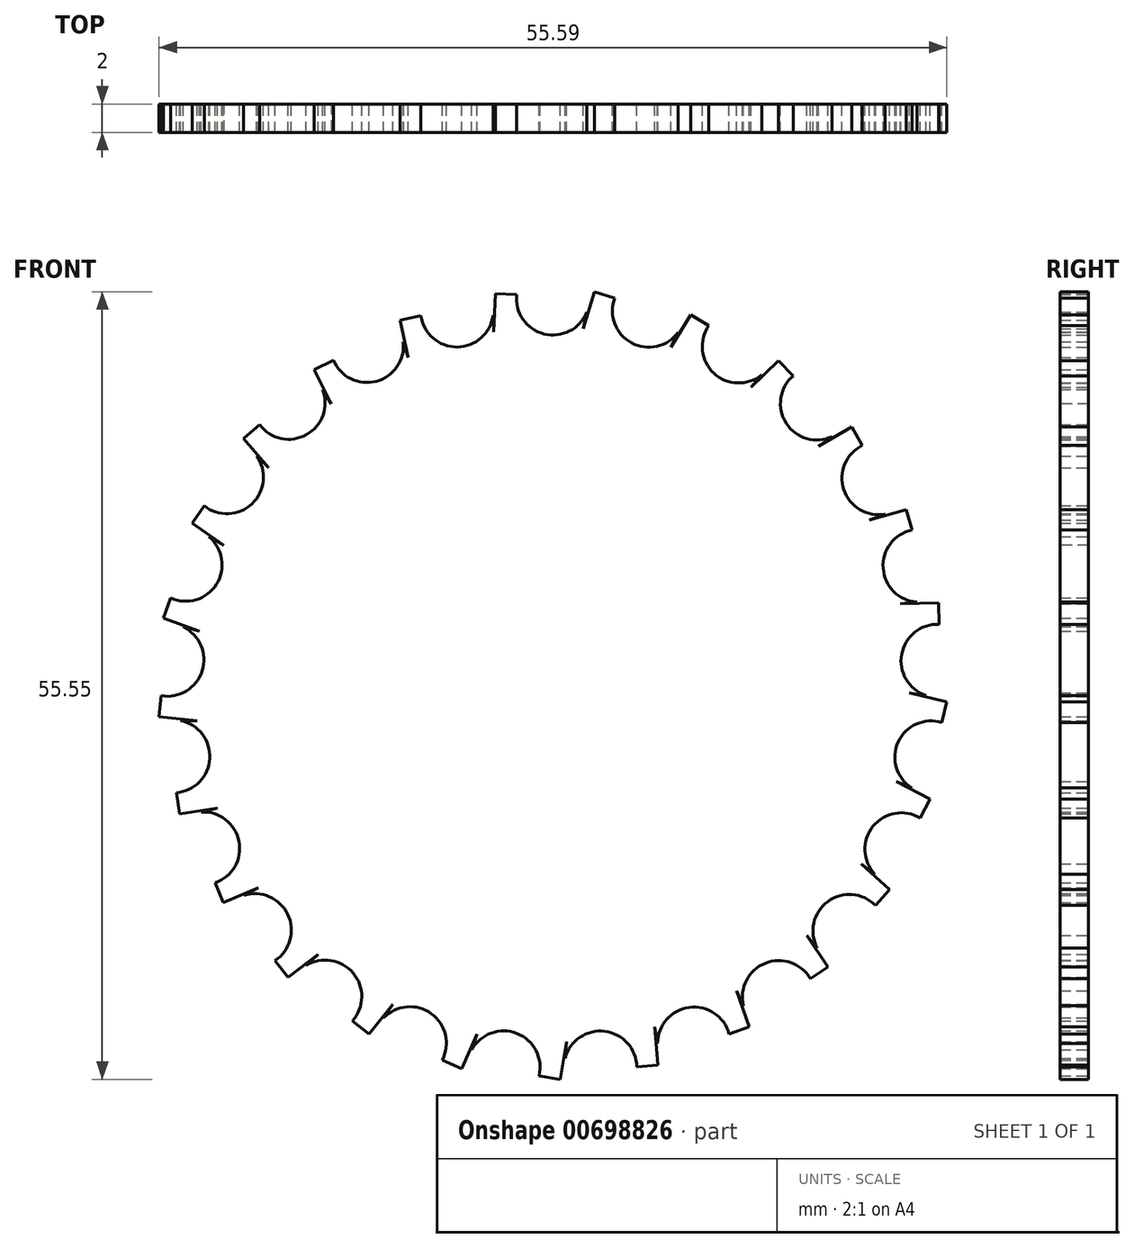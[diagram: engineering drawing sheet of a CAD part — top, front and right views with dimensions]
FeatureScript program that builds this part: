
annotation { "Feature Type Name" : "Feature", "Feature Type Description" : "" }
export const myFeature = defineFeature(function(context is Context, id is Id, definition is map)
    precondition{}
    {
        {
            var Q0;
            Q0=qCreatedBy(makeId("Front.planeOp"),FACE);
            var sketch = newSketch(context, id + "F0", { "sketchPlane" : qUnion([Q0])});
            skArc(sketch, "E0", {"start": v(-24.57, 12.6) * mm, "mid": v(-21.2, 12.75) * mm, "end": v(-20.88, 16.12) * mm});
            skLineSegment(sketch, "E1", {"start": v(-24.57, 12.6) * mm, "end": v(-25.43, 11.37) * mm});
            skLineSegment(sketch, "E2", {"start": v(-25.43, 11.37) * mm, "end": v(-22.14, 9.1) * mm});
            skLineSegment(sketch, "E3", {"start": v(-22.14, 9.1) * mm, "end": v(-18.72, 14.03) * mm});
            skLineSegment(sketch, "E4", {"start": v(-18.72, 14.03) * mm, "end": v(-20.88, 16.12) * mm});
            skCircle(sketch, "E5", {"center": v(0, 0) * mm, "radius": 1.38 * mm});
            skSolve(sketch);
        }
        {
            var Q0;
            Q0=makeQuery(id+"F0.imprint","IMPRINT",FACE,{"disambiguationData":[TD([[makeQuery(id+"F0.imprint","IMPRINT",EDGE,{"derivedFrom":sQuery(id+"F0.wireOp",EDGE,"E0")}),-1.0]])]});
            extrude(context, id + "F1", {"entities" : qUnion([Q0]), "depth" : 2 * mm, "offsetDistance" : 25 * mm});
        }
        {
            var Q0;
            Q0=makeQuery(id+"F1.opExtrude","SWEPT_BODY",BODY,{"disambiguationData":[OSD([sQuery(id+"F0.wireOp",EDGE,"E0"),sQuery(id+"F0.wireOp",EDGE,"E1"),sQuery(id+"F0.wireOp",EDGE,"E2"),sQuery(id+"F0.wireOp",EDGE,"E3"),sQuery(id+"F0.wireOp",EDGE,"E4")])]});
            var Q1;
            Q1=sQuery(id+"F0.wireOp",EDGE,"E5");
            circularPattern(context, id + "F2", {"entities" : qUnion([Q0]), "axis" : qUnion([Q1]), "angle" : 360 * degree, "instanceCount" : 25, "equalSpace" : true, "isCentered" : true});
        }
        {
            var Q0;
            Q0 = qSketchRegion(id + "F0", true);
            extrude(context, id + "F3", {"entities" : qUnion([Q0]), "operationType" : NewBodyOperationType.ADD, "depth" : 2 * mm, "offsetDistance" : 25 * mm});
        }
        {
            var Q0;
            Q0=qCreatedBy(makeId("Front.planeOp"),FACE);
            var sketch = newSketch(context, id + "F4", { "sketchPlane" : qUnion([Q0])});
            skCircle(sketch, "E6", {"center": v(0, 0) * mm, "radius": 24.18 * mm});
            skSolve(sketch);
        }
        {
            var Q0;
            Q0 = qSketchRegion(id + "F4", true);
            extrude(context, id + "F5", {"entities" : qUnion([Q0]), "operationType" : NewBodyOperationType.ADD, "depth" : 2 * mm, "offsetDistance" : 25 * mm});
        }
    });
